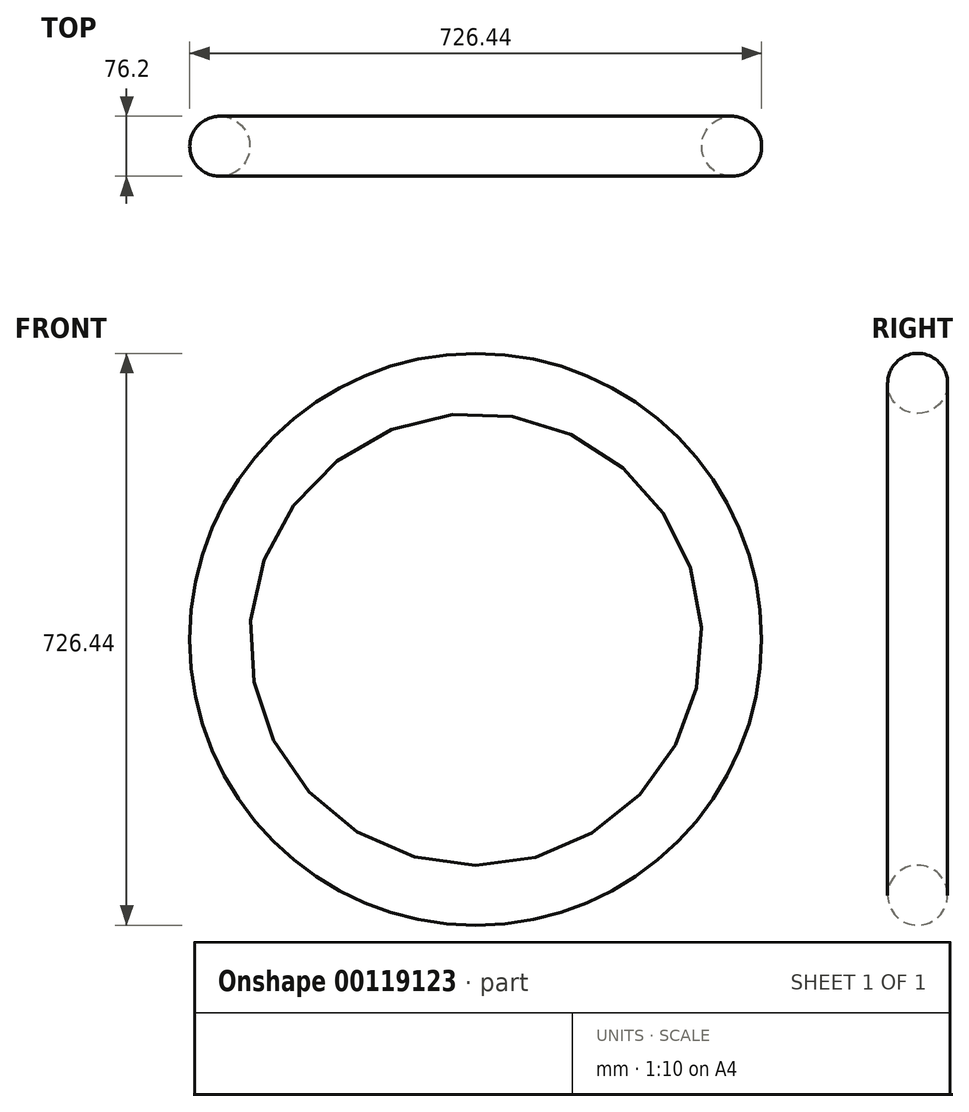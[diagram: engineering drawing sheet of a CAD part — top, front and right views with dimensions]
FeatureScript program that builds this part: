
annotation { "Feature Type Name" : "Feature", "Feature Type Description" : "" }
export const myFeature = defineFeature(function(context is Context, id is Id, definition is map)
    precondition{}
    {
        {
            var Q0;
            Q0=qCreatedBy(makeId("Top.planeOp"),FACE);
            var sketch = newSketch(context, id + "F0", { "sketchPlane" : qUnion([Q0])});
            skCircle(sketch, "E0", {"center": v(-325.12, 0) * mm, "radius": 38.1 * mm});
            skLineSegment(sketch, "E1", {"start": v(-325.12, 0) * mm, "end": v(0, 0) * mm, "construction": true});
            skLineSegment(sketch, "E2", {"start": v(0, 0) * mm, "end": v(0, 48.1) * mm, "construction": true});
            skSolve(sketch);
        }
        {
            var Q0;
            Q0=makeQuery(id+"F0.imprint","IMPRINT",FACE,{"disambiguationData":[TD([[makeQuery(id+"F0.imprint","IMPRINT",EDGE,{"derivedFrom":sQuery(id+"F0.wireOp",EDGE,"E0")}),1.0]])]});
            var Q1;
            Q1=sQuery(id+"F0.wireOp",EDGE,"E2");
            revolve(context, id + "F1", {"entities" : qUnion([Q0]), "axis" : qUnion([Q1]), "revolveType" : RevolveType.FULL});
        }
    });
